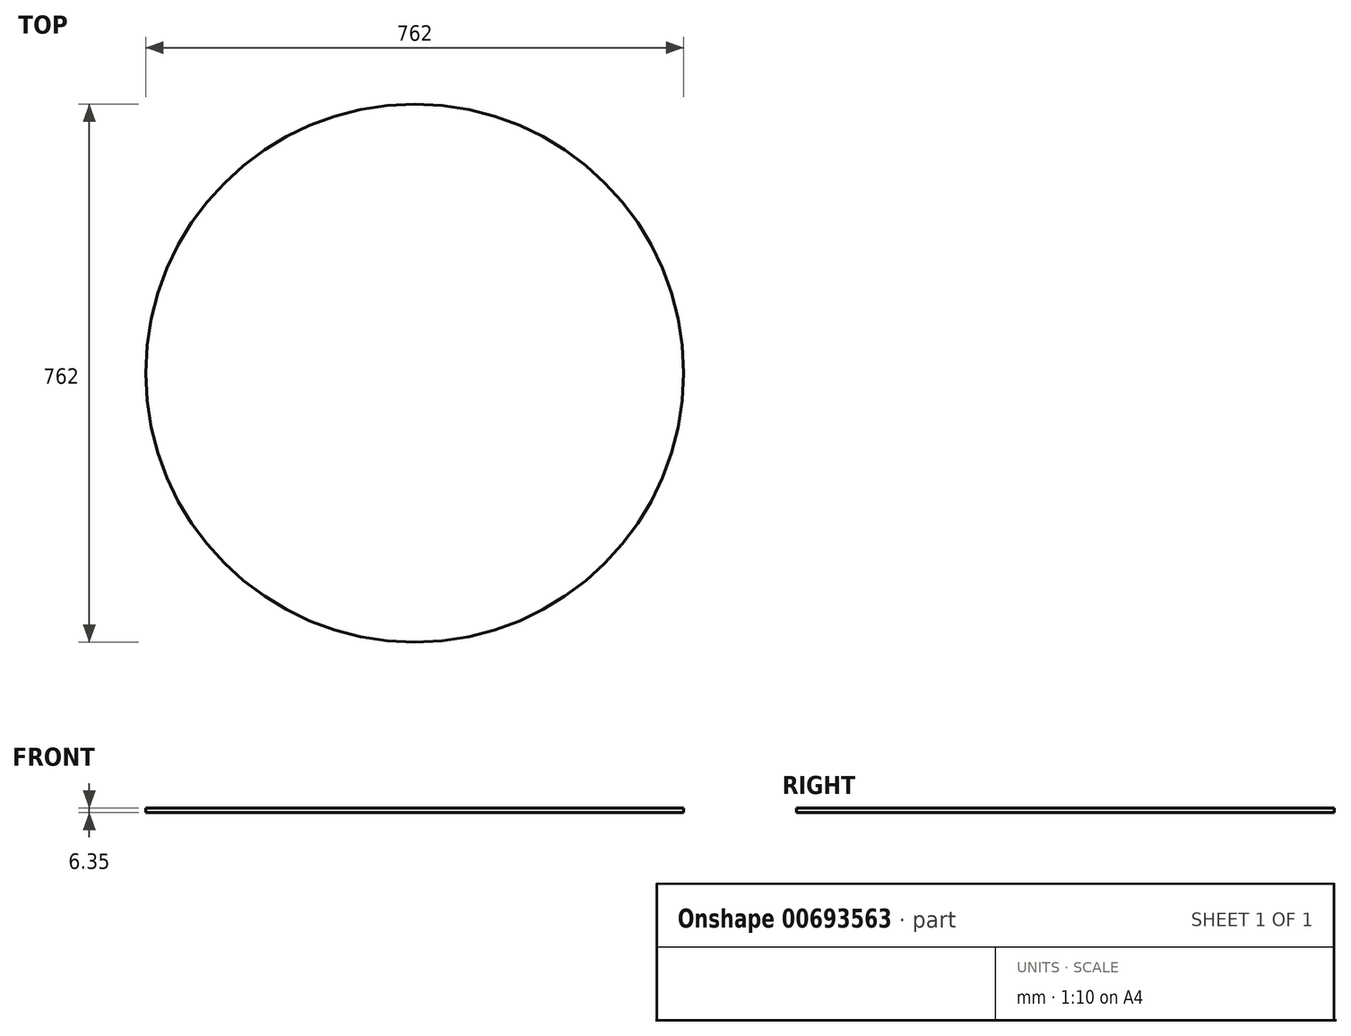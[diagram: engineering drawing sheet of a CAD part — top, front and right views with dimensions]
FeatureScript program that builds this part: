
annotation { "Feature Type Name" : "Feature", "Feature Type Description" : "" }
export const myFeature = defineFeature(function(context is Context, id is Id, definition is map)
    precondition{}
    {
        {
            var Q0;
            Q0=qCreatedBy(makeId("Top.planeOp"),FACE);
            var sketch = newSketch(context, id + "F0", { "sketchPlane" : qUnion([Q0])});
            skCircle(sketch, "E0", {"center": v(0, 0) * mm, "radius": 381 * mm});
            skSolve(sketch);
        }
        {
            var Q0;
            Q0=makeQuery(id+"F0.imprint","IMPRINT",FACE,{"disambiguationData":[TD([[makeQuery(id+"F0.imprint","IMPRINT",EDGE,{"derivedFrom":sQuery(id+"F0.wireOp",EDGE,"E0")}),1.0]])]});
            var Q1;
            Q1=sQuery(id+"F0.wireOp",EDGE,"E0");
            extrude(context, id + "F1", {"entities" : qUnion([Q0]), "surfaceEntities" : qUnion([Q1]), "depth" : 6.35 * mm, "offsetDistance" : 25 * mm});
        }
    });
